# Revit family: ES-LCD
name_source: partatom
category: Mechanical Equipment
revit_build: Autodesk Revit 2018 (Build: 20170223_1515(x64)
units: mm (PartAtom-declared; Revit-internal decimal feet)

## family parameters
Always vertical = No
Cut with Voids When Loaded = No
OmniClass Number = 23.75.00.00
OmniClass Title = Climate Control (HVAC)
Part Type = Normal
Room Calculation Point = No
Round Connector Dimension = Use Diameter
Shared = No
Work Plane-Based = Yes

## types (4) — shared parameters
Classification.Uniclass.Pr.Description = Fans
Classification.Uniclass.Pr.Number = Pr_65_67_29
Default Elevation = 1219 mm
Fax Number = +44(0)2920-858-222
IFCExportAs = IfcFanType
Manufacturer = Nuaire
Manufacturer Name = Nuaire
Maximum Ambient Temperature = 40 °C
OmniClass Number = 23-33 31 19
OmniClass Title = Fans
Postcode = CF83 1NA
Revit Family Last Revised = 23/04/21
Telephone Number = +44(0)2920-858-200
URL = http://www.nuaire.co.uk
VAT Registration Number = 877308
Weatherproof or Internal Only = Internal
Weight = 0.25 kg

## per-type parameters (varying)
| type | Catalogue Pages | Description | Height | I&M Manual | Type Comments | Unit Description | Warranty Period | Width |
| ES-LCD |  | Wall Mounted LCD Fan Controller | 85 mm | http://www.nuaire.info | Wall Mounted LCD Fan Controller | Wall Mounted LCD Fan Controller | 1 Years | 145 mm |
| ES-UCFH | http://www.nuaire.info | Wall Mounted Low Voltage Fan Speed Controller - Ventilation and Heating | 75 mm | http://nuaire.info | Wall Mounted Low Voltage Fan Speed Controller - Ventilation and Heating | Wall Mounted Low Voltage Fan Speed Controller - Ventilation and Heating | 3 Years | 163 mm |
| ES-UCFHC | http://www.nuaire.info | Wall Mounted Low Voltage Fan Speed Controller - Ventilation, Heating and Cooling | 75 mm | http://nuaire.info | Wall Mounted Low Voltage Fan Speed Controller - Ventilation, Heating and Cooling | Wall Mounted Low Voltage Fan Speed Controller - Ventilation, Heating and Cooling | 3 Years | 163 mm |
| ES-LCD2 |  | Wall Mounted LCD Fan Controller | 85 mm | http://www.nuaire.info | Wall Mounted LCD Fan Controller | Wall Mounted LCD Fan Controller | 1 Years | 145 mm |

note: column(s) folded — value = type name in every type: Model, Nuaire Model Code

## geometry (parser evidence)
native form markers: Blend x2, Sweep x3
no freeform markers — native parametric forms only
